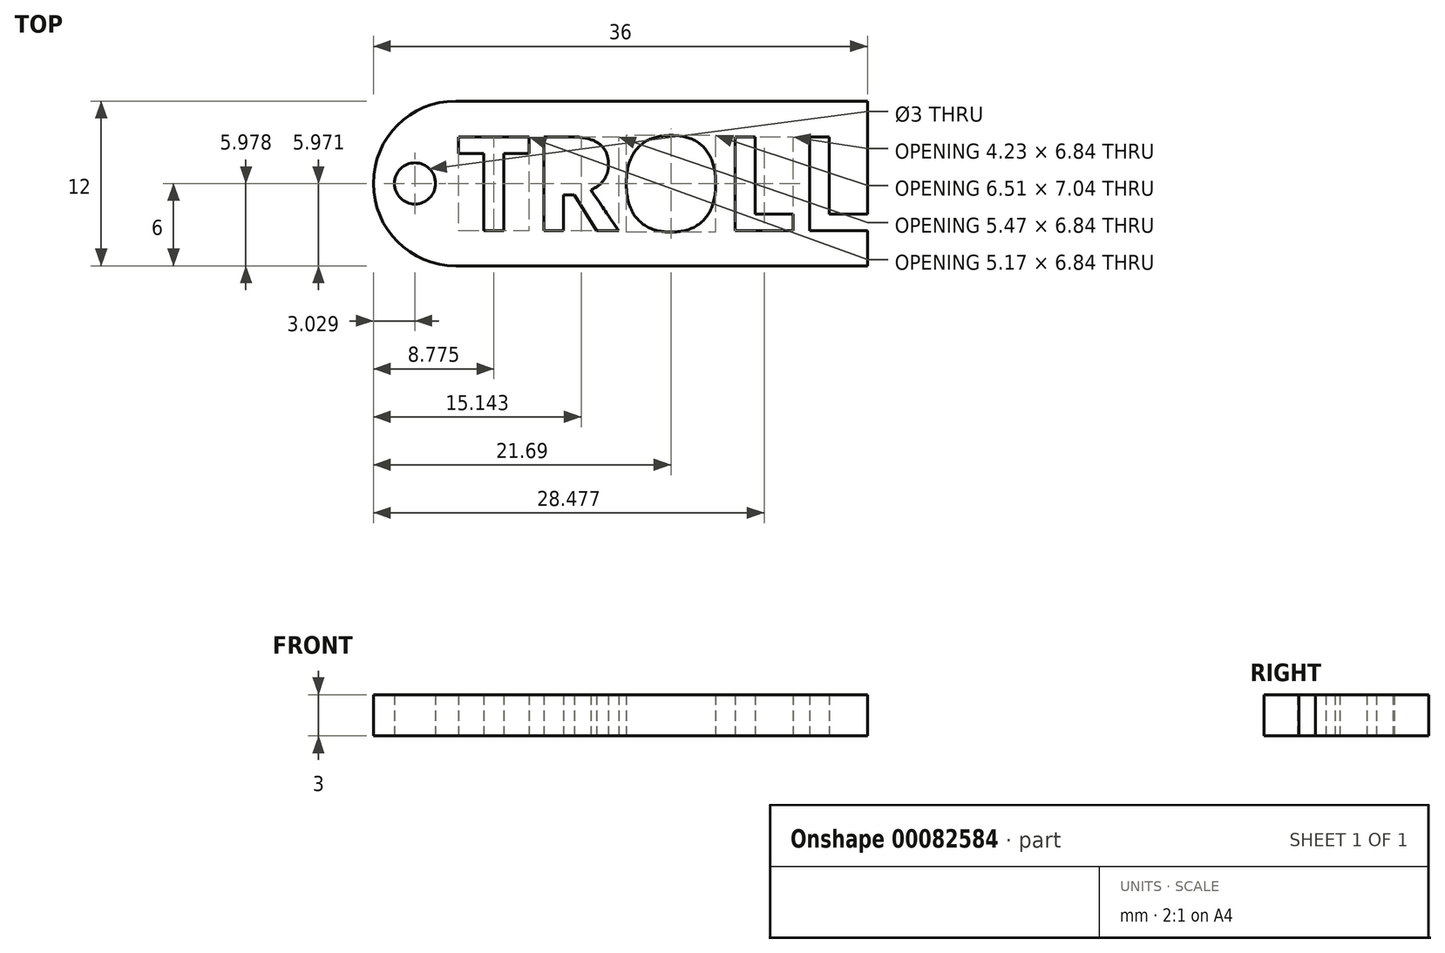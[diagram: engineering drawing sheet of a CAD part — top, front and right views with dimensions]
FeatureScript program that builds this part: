
annotation { "Feature Type Name" : "Feature", "Feature Type Description" : "" }
export const myFeature = defineFeature(function(context is Context, id is Id, definition is map)
    precondition{}
    {
        {
            var Q0;
            Q0=qCreatedBy(makeId("Top.planeOp"),FACE);
            var sketch = newSketch(context, id + "F0", { "sketchPlane" : qUnion([Q0])});
            skLineSegment(sketch, "E0.bottom", {"start": v(-15, 6) * mm, "end": v(15, 6) * mm});
            skLineSegment(sketch, "E0.top", {"start": v(-15, -6) * mm, "end": v(15, -6) * mm});
            skLineSegment(sketch, "E0.left", {"start": v(-15, 6) * mm, "end": v(-15, -6) * mm});
            skLineSegment(sketch, "E0.right", {"start": v(15, 6) * mm, "end": v(15, -6) * mm});
            skPoint(sketch, "E0.middle", {"position": v(0, 0) * mm});
            skArc(sketch, "E1", {"start": v(-15, 6) * mm, "mid": v(-21, 0) * mm, "end": v(-15, -6) * mm});
            skArc(sketch, "E2", {"start": v(15, 6) * mm, "mid": v(21, 0) * mm, "end": v(15, -6) * mm});
            skText(sketch, "E3", { "text": "TROLL", "fontName": "OpenSans-Bold.ttf"});
            skPoint(sketch, "E4", {"position": v(0, 6) * mm});
            skCircle(sketch, "E5", {"center": v(-17.97, 0) * mm, "radius": 1.5 * mm});
            const initialGuessF0  = {"E3": [-0.015, -0.00345, 1, 0, 0.0069]};
            skSetInitialGuess(sketch, initialGuessF0);
            skSolve(sketch);
        }
        {
            var Q0;
            Q0=makeQuery(id+"F0.imprint","IMPRINT",FACE,{"disambiguationData":[TD([[makeQuery(id+"F0.imprint","IMPRINT",EDGE,{"derivedFrom":sQuery(id+"F0.wireOp",EDGE,"E0.left")}),-1.0]])]});
            var Q1;
            {var subQ0=sQuery(id+"F0.wireOp",EDGE,"E2");Q1=makeQuery(id+"F0.imprint","IMPRINT",FACE,{"disambiguationData":[TD([[makeQuery(id+"F0.imprint","IMPRINT",EDGE,{"derivedFrom":subQ0}),-1.0]])]});}
            var Q2;
            {var subQ0=sQuery(id+"F0.wireOp",EDGE,"E0.bottom");Q2=makeQuery(id+"F0.imprint","IMPRINT",FACE,{"disambiguationData":[TD([[makeQuery(id+"F0.imprint","IMPRINT",EDGE,{"derivedFrom":subQ0}),-1.0]])]});}
            extrude(context, id + "F1", {"entities" : qUnion([Q0, Q1, Q2]), "depth" : 3 * mm});
        }
    });
